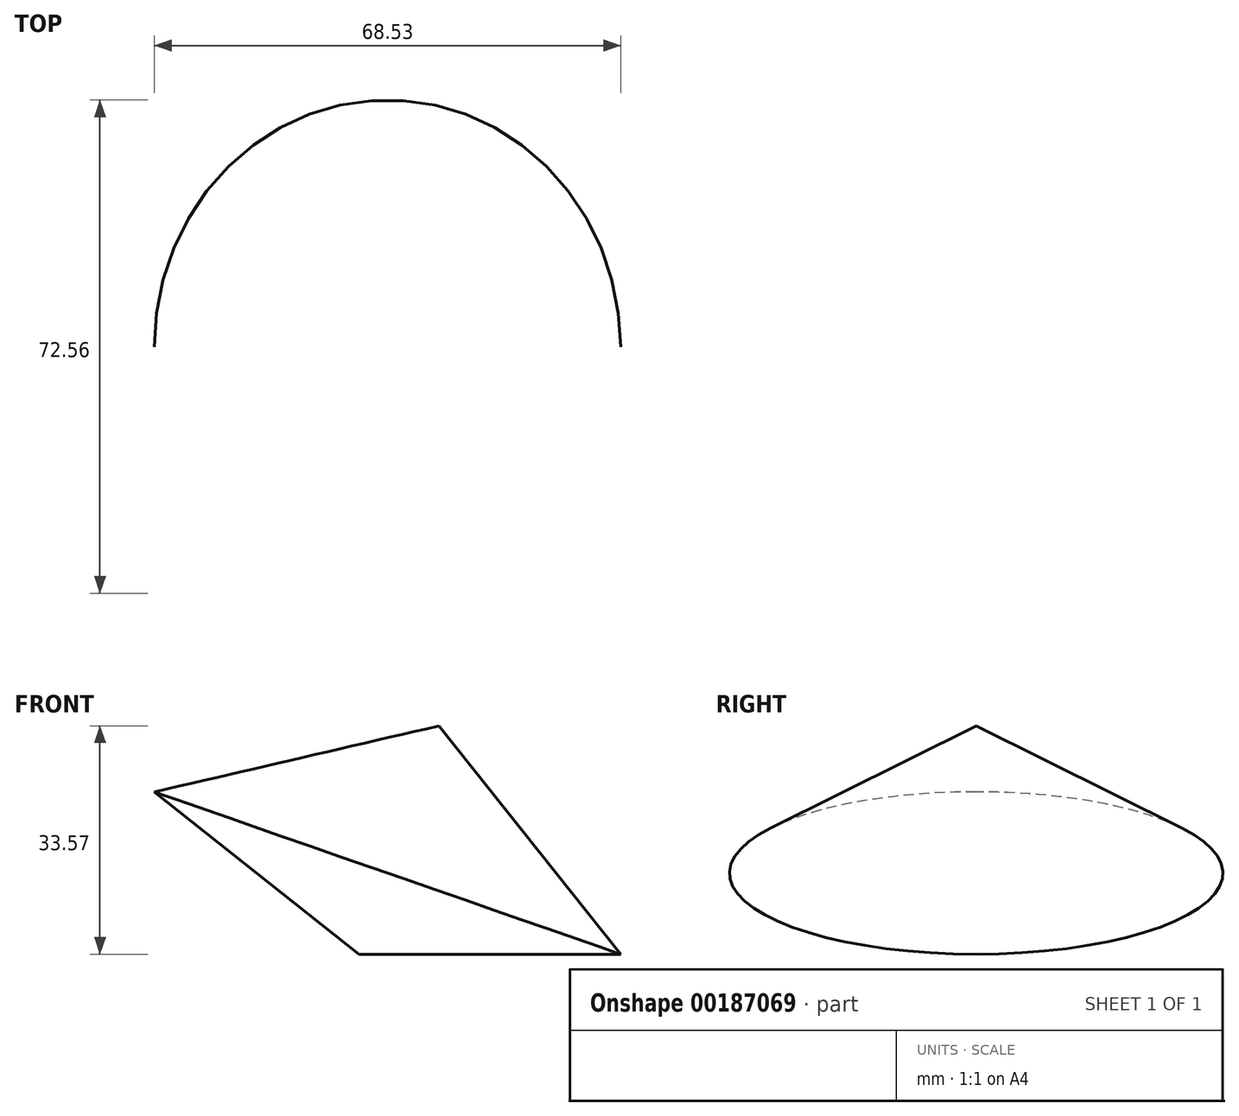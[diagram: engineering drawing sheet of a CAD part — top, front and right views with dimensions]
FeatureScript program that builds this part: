
annotation { "Feature Type Name" : "Feature", "Feature Type Description" : "" }
export const myFeature = defineFeature(function(context is Context, id is Id, definition is map)
    precondition{}
    {
        {
            var Q0;
            Q0=qCreatedBy(makeId("Front.planeOp"),FACE);
            var sketch = newSketch(context, id + "F0", { "sketchPlane" : qUnion([Q0])});
            skLineSegment(sketch, "E0", {"start": v(0, 0) * mm, "end": v(38.42, 0) * mm});
            skLineSegment(sketch, "E1", {"start": v(38.42, 0) * mm, "end": v(11.7, 33.57) * mm});
            skLineSegment(sketch, "E2", {"start": v(11.7, 33.57) * mm, "end": v(0, 0) * mm});
            skSolve(sketch);
        }
        {
            var Q0;
            Q0=makeQuery(id+"F0.imprint","IMPRINT",FACE,{"disambiguationData":[TD([[makeQuery(id+"F0.imprint","IMPRINT",EDGE,{"derivedFrom":sQuery(id+"F0.wireOp",EDGE,"E0")}),1.0]])]});
            var Q1;
            Q1=sQuery(id+"F0.wireOp",EDGE,"E2");
            revolve(context, id + "F1", {"entities" : qUnion([Q0]), "axis" : qUnion([Q1]), "revolveType" : RevolveType.FULL});
        }
    });
